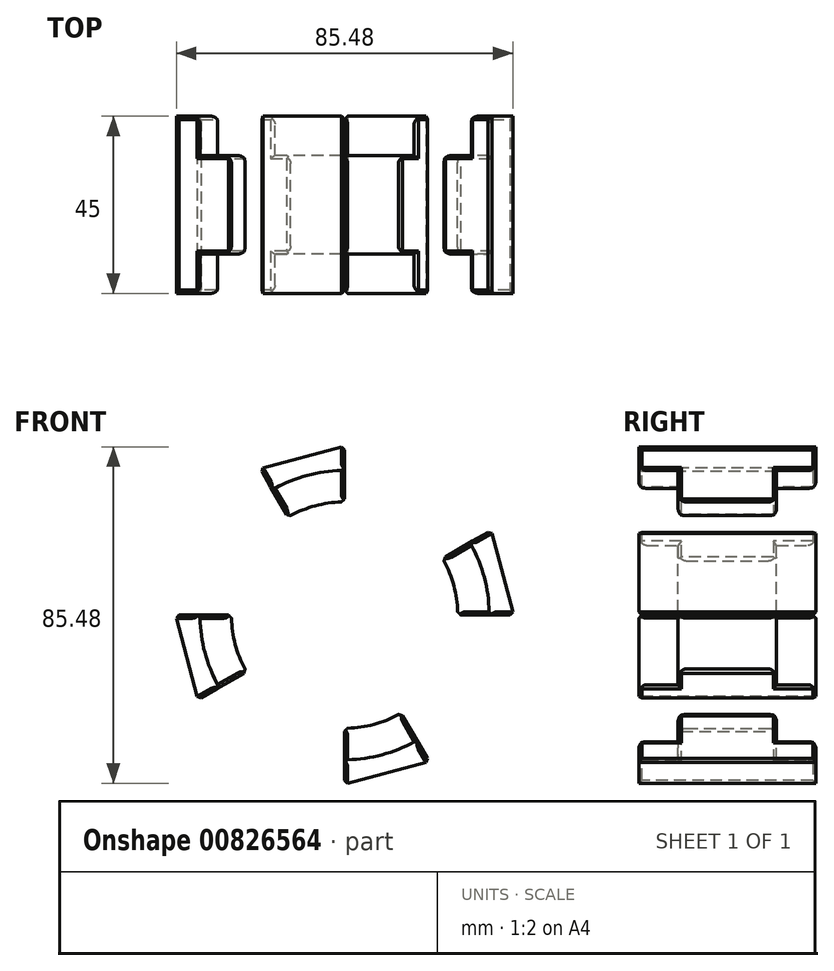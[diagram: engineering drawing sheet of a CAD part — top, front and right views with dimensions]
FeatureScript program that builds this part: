
annotation { "Feature Type Name" : "Feature", "Feature Type Description" : "" }
export const myFeature = defineFeature(function(context is Context, id is Id, definition is map)
    precondition{}
    {
        {
            var Q0;
            Q0=qCreatedBy(makeId("Front.planeOp"),FACE);
            var sketch = newSketch(context, id + "F0", { "sketchPlane" : qUnion([Q0])});
            skPoint(sketch, "E0", {"position": v(36.75, 0) * mm});
            skLineSegment(sketch, "E1", {"start": v(36.75, 0) * mm, "end": v(0, 0) * mm, "construction": true});
            skLineSegment(sketch, "E2", {"start": v(31.83, 18.38) * mm, "end": v(0, 0) * mm, "construction": true});
            skLineSegment(sketch, "E3", {"start": v(31.83, 18.38) * mm, "end": v(38.75, 22.38) * mm});
            skLineSegment(sketch, "E4", {"start": v(36.75, 0) * mm, "end": v(44.75, 0) * mm});
            skArc(sketch, "E5", {"start": v(36.75, 0) * mm, "mid": v(35.5, 9.51) * mm, "end": v(31.83, 18.38) * mm});
            skArc(sketch, "E6", {"start": v(31.83, 18.38) * mm, "mid": v(-35.5, -9.51) * mm, "end": v(36.75, 0) * mm, "construction": true});
            skLineSegment(sketch, "E7", {"start": v(44.75, 0) * mm, "end": v(44.75, 0) * mm});
            skArc(sketch, "E8", {"start": v(38.75, 22.38) * mm, "mid": v(-43.23, -11.58) * mm, "end": v(44.75, 0) * mm, "construction": true});
            skArc(sketch, "E9", {"start": v(44.75, 0) * mm, "mid": v(43.23, 11.58) * mm, "end": v(38.75, 22.38) * mm});
            skSolve(sketch);
        }
        {
            var Q0;
            Q0=makeQuery(id+"F0.imprint","IMPRINT",FACE,{"disambiguationData":[TD([[makeQuery(id+"F0.imprint","IMPRINT",EDGE,{"derivedFrom":sQuery(id+"F0.wireOp",EDGE,"E3")}),-1.0]])]});
            var Q1;
            Q1 = qConstructionFilter(qBodyType(qCreatedBy(id + "F0" ,EDGE), BodyType.WIRE), ConstructionObject.NO);
            extrude(context, id + "F1", {"entities" : qUnion([Q0]), "surfaceEntities" : qUnion([Q1]), "endBound" : BoundingType.SYMMETRIC, "depth" : 45 * mm, "offsetDistance" : 25 * mm});
        }
        {
            var Q0;
            Q0=qCreatedBy(makeId("Front.planeOp"),FACE);
            var sketch = newSketch(context, id + "F2", { "sketchPlane" : qUnion([Q0])});
            skArc(sketch, "E10.0", {"start": v(36.75, 0) * mm, "mid": v(35.5, 9.51) * mm, "end": v(31.83, 18.38) * mm});
            skLineSegment(sketch, "E11", {"start": v(0, 0) * mm, "end": v(24.9, 14.38) * mm, "construction": true});
            skLineSegment(sketch, "E12", {"start": v(0, 0) * mm, "end": v(28.75, 0) * mm, "construction": true});
            skArc(sketch, "E13", {"start": v(28.75, 0) * mm, "mid": v(27.77, 7.44) * mm, "end": v(24.9, 14.38) * mm});
            skLineSegment(sketch, "E14", {"start": v(36.75, 0) * mm, "end": v(36.75, 0) * mm});
            skLineSegment(sketch, "E15", {"start": v(28.75, 0) * mm, "end": v(36.75, 0) * mm});
            skLineSegment(sketch, "E16", {"start": v(24.9, 14.38) * mm, "end": v(31.83, 18.38) * mm});
            skLineSegment(sketch, "E17", {"start": v(31.83, 18.38) * mm, "end": v(31.83, 18.38) * mm});
            skSolve(sketch);
        }
        {
            var Q0;
            Q0 = qSketchRegion(id + "F2", true);
            extrude(context, id + "F3", {"entities" : qUnion([Q0]), "operationType" : NewBodyOperationType.ADD, "endBound" : BoundingType.SYMMETRIC, "depth" : 25 * mm, "offsetDistance" : 25 * mm});
        }
        {
            var Q0;
            Q0=makeQuery(id+"F3.boolean.opBoolean","MERGE",FACE,{"derivedFrom":[makeQuery(id+"F1.opExtrude","SWEPT_FACE",FACE,{"disambiguationData":[OSD([sQuery(id+"F0.wireOp",EDGE,"E4")])]}),makeQuery(id+"F3.opExtrude","SWEPT_FACE",FACE,{"disambiguationData":[OSD([sQuery(id+"F2.wireOp",EDGE,"E15")])]})]});
            var Q1;
            Q1=makeQuery(id+"F3.boolean.opBoolean","MERGE",FACE,{"derivedFrom":[makeQuery(id+"F1.opExtrude","SWEPT_FACE",FACE,{"disambiguationData":[OSD([sQuery(id+"F0.wireOp",EDGE,"E3")])]}),makeQuery(id+"F3.opExtrude","SWEPT_FACE",FACE,{"disambiguationData":[OSD([sQuery(id+"F2.wireOp",EDGE,"E16")])]})]});
            chamfer(context, id + "F4", {"entities" : qUnion([Q0, Q1]), "width" : 0.8 * mm, "tangentPropagation" : true});
        }
        {
            var Q0;
            Q0=makeQuery(id+"F3.opExtrude","CAP_EDGE",EDGE,{"disambiguationData":[OSD([sQuery(id+"F2.wireOp",EDGE,"E13")])],"isStart":false});
            var Q1;
            Q1=makeQuery(id+"F1.opExtrude","CAP_EDGE",EDGE,{"disambiguationData":[OSD([sQuery(id+"F0.wireOp",EDGE,"E5")])],"isStart":false});
            var Q2;
            Q2=makeQuery(id+"F1.opExtrude","CAP_EDGE",EDGE,{"disambiguationData":[OSD([sQuery(id+"F0.wireOp",EDGE,"E9")])],"isStart":false});
            var Q3;
            Q3=makeQuery(id+"F1.opExtrude","CAP_EDGE",EDGE,{"disambiguationData":[OSD([sQuery(id+"F0.wireOp",EDGE,"E9")])],"isStart":true});
            var Q4;
            Q4=makeQuery(id+"F1.opExtrude","CAP_EDGE",EDGE,{"disambiguationData":[OSD([sQuery(id+"F0.wireOp",EDGE,"E5")])],"isStart":true});
            var Q5;
            Q5=makeQuery(id+"F3.opExtrude","CAP_EDGE",EDGE,{"disambiguationData":[OSD([sQuery(id+"F2.wireOp",EDGE,"E13")])],"isStart":true});
            fillet(context, id + "F5", {"entities" : qUnion([Q0, Q1, Q2, Q3, Q4, Q5]), "radius" : 2 * mm, "tangentPropagation" : true, "allowEdgeOverflow" : false});
        }
        {
            var Q0;
            Q0=qCreatedBy(makeId("Top.planeOp"),FACE);
            var sketch = newSketch(context, id + "F6", { "sketchPlane" : qUnion([Q0])});
            skLineSegment(sketch, "E18", {"start": v(0, -40) * mm, "end": v(0, 40) * mm, "construction": true});
            skSolve(sketch);
        }
        {
            var Q0;
            Q0=makeQuery(id+"F1.opExtrude","CAP_FACE",FACE,{"disambiguationData":[OSD([sQuery(id+"F0.wireOp",EDGE,"E3"),sQuery(id+"F0.wireOp",EDGE,"E4"),sQuery(id+"F0.wireOp",EDGE,"E5"),sQuery(id+"F0.wireOp",EDGE,"E9")])],"isStart":false});
            var sketch = newSketch(context, id + "F7", { "sketchPlane" : qUnion([Q0])});
            skLineSegment(sketch, "E19", {"start": v(37.42, 20.68) * mm, "end": v(42.74, 0.8) * mm});
            skLineSegment(sketch, "E20", {"start": v(42.74, 0.8) * mm, "end": v(37.55, -4.79) * mm});
            skLineSegment(sketch, "E21", {"start": v(37.55, -4.79) * mm, "end": v(62.73, 6.04) * mm});
            skLineSegment(sketch, "E22", {"start": v(62.73, 6.04) * mm, "end": v(46.87, 30.18) * mm});
            skLineSegment(sketch, "E23", {"start": v(46.87, 30.18) * mm, "end": v(34.72, 21.63) * mm});
            skLineSegment(sketch, "E24", {"start": v(34.72, 21.63) * mm, "end": v(37.42, 20.68) * mm});
            skSolve(sketch);
        }
        {
            var Q0;
            Q0 = qSketchRegion(id + "F7", true);
            extrude(context, id + "F8", {"entities" : qUnion([Q0]), "operationType" : NewBodyOperationType.REMOVE, "endBound" : BoundingType.THROUGH_ALL, "oppositeDirection" : true, "depth" : 25 * mm, "offsetDistance" : 25 * mm});
        }
        {
            var Q0;
            Q0=makeQuery(id+"F1.opExtrude","SWEPT_BODY",BODY,{"disambiguationData":[OSD([sQuery(id+"F0.wireOp",EDGE,"E3"),sQuery(id+"F0.wireOp",EDGE,"E4"),sQuery(id+"F0.wireOp",EDGE,"E5"),sQuery(id+"F0.wireOp",EDGE,"E9")])]});
            var Q1;
            Q1=sQuery(id+"F6.wireOp",EDGE,"E18");
            circularPattern(context, id + "F9", {"entities" : qUnion([Q0]), "axis" : qUnion([Q1]), "angle" : 360 * degree, "instanceCount" : 4, "equalSpace" : true});
        }
    });
